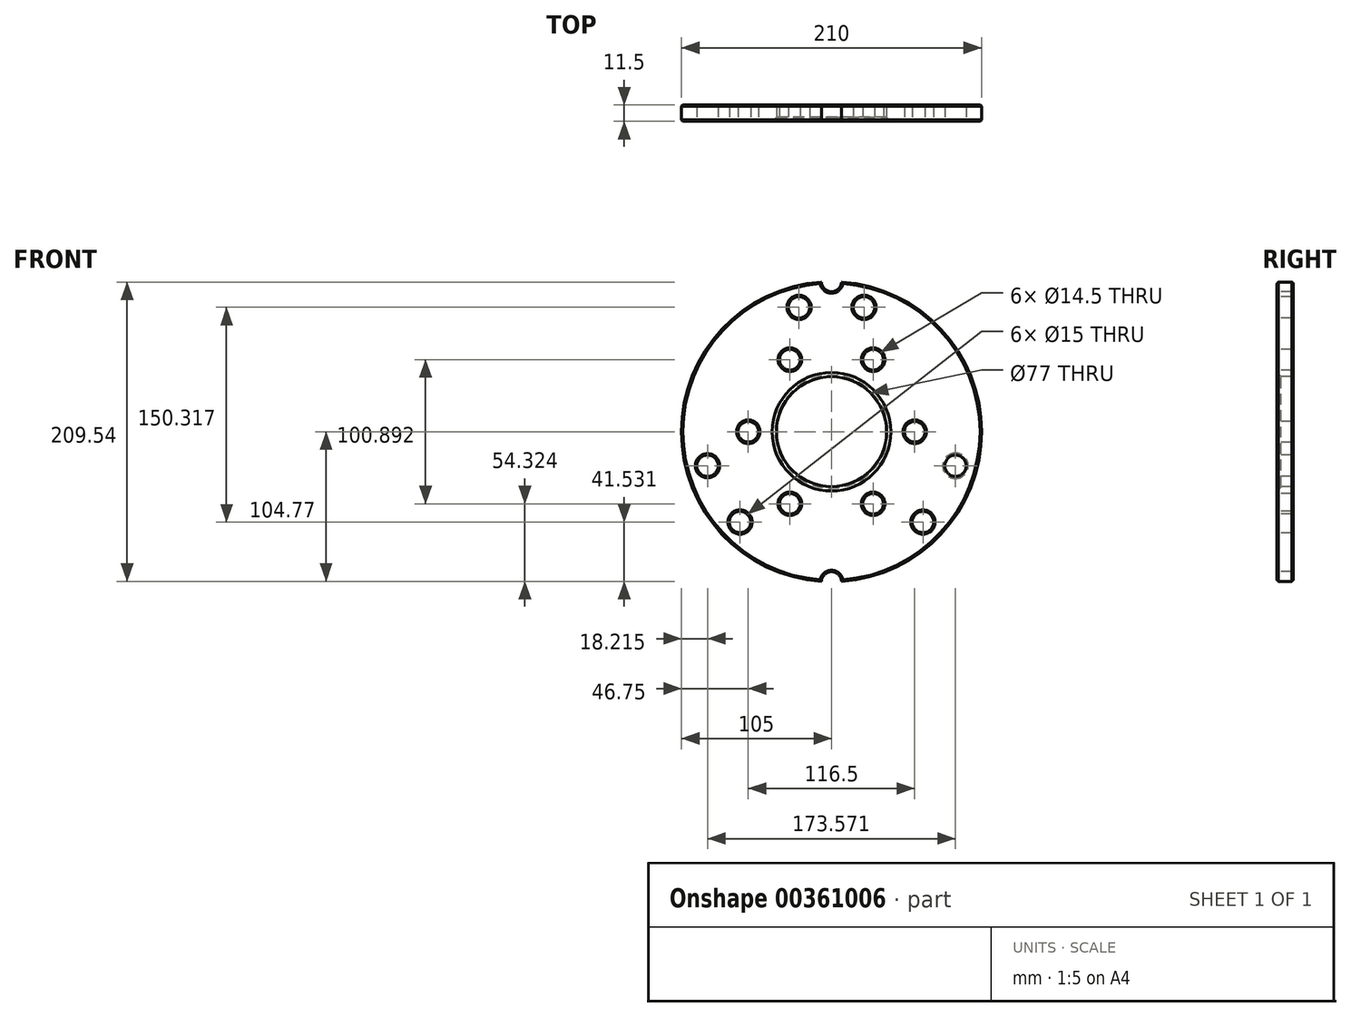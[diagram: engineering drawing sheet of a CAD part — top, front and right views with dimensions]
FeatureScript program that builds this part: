
annotation { "Feature Type Name" : "Feature", "Feature Type Description" : "" }
export const myFeature = defineFeature(function(context is Context, id is Id, definition is map)
    precondition{}
    {
        {
            var Q0;
            Q0=qCreatedBy(makeId("Front.planeOp"),FACE);
            var sketch = newSketch(context, id + "F0", { "sketchPlane" : qUnion([Q0])});
            skArc(sketch, "E0", {"start": v(-7, 104.77) * mm, "mid": v(-105, 0) * mm, "end": v(-7, -104.77) * mm});
            skCircle(sketch, "E1", {"center": v(0, 0) * mm, "radius": 38.5 * mm});
            skCircle(sketch, "E2", {"center": v(-29.12, 50.45) * mm, "radius": 7.25 * mm});
            skCircle(sketch, "E3.1.0", {"center": v(-58.25, 0) * mm, "radius": 7.25 * mm});
            skCircle(sketch, "E3.2.0", {"center": v(-29.13, -50.45) * mm, "radius": 7.25 * mm});
            skCircle(sketch, "E3.3.0", {"center": v(29.12, -50.45) * mm, "radius": 7.25 * mm});
            skCircle(sketch, "E3.4.0", {"center": v(58.25, 0) * mm, "radius": 7.25 * mm});
            skCircle(sketch, "E3.5.0", {"center": v(29.12, 50.45) * mm, "radius": 7.25 * mm});
            skArc(sketch, "E4", {"start": v(-7, 104.77) * mm, "mid": v(0, 98) * mm, "end": v(7, 104.77) * mm});
            skArc(sketch, "E5", {"start": v(7, -104.77) * mm, "mid": v(0, -98) * mm, "end": v(-7, -104.77) * mm});
            skArc(sketch, "E6.trimOffspring", {"start": v(7, -104.77) * mm, "mid": v(105, 0) * mm, "end": v(7, 104.77) * mm});
            skPoint(sketch, "E7.start.orphan", {"position": v(-105, 0) * mm});
            skCircle(sketch, "E8", {"center": v(-22.75, 87.08) * mm, "radius": 7.5 * mm});
            skCircle(sketch, "E9.1.0", {"center": v(-64.04, -63.24) * mm, "radius": 7.5 * mm});
            skCircle(sketch, "E9.2.0", {"center": v(86.79, -23.84) * mm, "radius": 7.5 * mm});
            skCircle(sketch, "E10", {"center": v(22.75, 87.08) * mm, "radius": 7.5 * mm});
            skCircle(sketch, "E11.1.0", {"center": v(-86.79, -23.84) * mm, "radius": 7.5 * mm});
            skCircle(sketch, "E11.2.0", {"center": v(64.04, -63.24) * mm, "radius": 7.5 * mm});
            skSolve(sketch);
        }
        {
            var Q0;
            Q0=makeQuery(id+"F0.imprint","IMPRINT",FACE,{"disambiguationData":[TD([[makeQuery(id+"F0.imprint","IMPRINT",EDGE,{"derivedFrom":sQuery(id+"F0.wireOp",EDGE,"E0")}),1.0]])]});
            extrude(context, id + "F1", {"entities" : qUnion([Q0]), "oppositeDirection" : true, "depth" : 11.5 * mm});
        }
        {
            var Q0;
            Q0=makeQuery(id+"F1.opExtrude","CAP_EDGE",EDGE,{"disambiguationData":[OSD([sQuery(id+"F0.wireOp",EDGE,"E1")])],"isStart":true});
            chamfer(context, id + "F2", {"entities" : qUnion([Q0]), "chamferType" : ChamferType.OFFSET_ANGLE, "width" : 3 * mm, "oppositeDirection" : false, "angle" : 45 * degree, "tangentPropagation" : true});
        }
        {
            var Q0;
            Q0=makeQuery(id+"F1.opExtrude","CAP_EDGE",EDGE,{"disambiguationData":[OSD([sQuery(id+"F0.wireOp",EDGE,"E2")])],"isStart":true});
            var Q1;
            Q1=makeQuery(id+"F1.opExtrude","CAP_EDGE",EDGE,{"disambiguationData":[OSD([sQuery(id+"F0.wireOp",EDGE,"E3.5.0")])],"isStart":true});
            var Q2;
            Q2=makeQuery(id+"F1.opExtrude","CAP_EDGE",EDGE,{"disambiguationData":[OSD([sQuery(id+"F0.wireOp",EDGE,"E9.2.0")])],"isStart":false});
            var Q3;
            Q3=makeQuery(id+"F1.opExtrude","CAP_EDGE",EDGE,{"disambiguationData":[OSD([sQuery(id+"F0.wireOp",EDGE,"E3.3.0")])],"isStart":true});
            var Q4;
            Q4=makeQuery(id+"F1.opExtrude","CAP_EDGE",EDGE,{"disambiguationData":[OSD([sQuery(id+"F0.wireOp",EDGE,"E3.2.0")])],"isStart":true});
            var Q5;
            Q5=makeQuery(id+"F1.opExtrude","CAP_EDGE",EDGE,{"disambiguationData":[OSD([sQuery(id+"F0.wireOp",EDGE,"E9.1.0")])],"isStart":true});
            var Q6;
            Q6=makeQuery(id+"F1.opExtrude","CAP_EDGE",EDGE,{"disambiguationData":[OSD([sQuery(id+"F0.wireOp",EDGE,"E5")])],"isStart":true});
            var Q7;
            Q7=makeQuery(id+"F1.opExtrude","CAP_EDGE",EDGE,{"disambiguationData":[OSD([sQuery(id+"F0.wireOp",EDGE,"E11.2.0")])],"isStart":true});
            var Q8;
            Q8=makeQuery(id+"F1.opExtrude","CAP_EDGE",EDGE,{"disambiguationData":[OSD([sQuery(id+"F0.wireOp",EDGE,"E11.1.0")])],"isStart":true});
            var Q9;
            Q9=makeQuery(id+"F1.opExtrude","CAP_EDGE",EDGE,{"disambiguationData":[OSD([sQuery(id+"F0.wireOp",EDGE,"E3.1.0")])],"isStart":true});
            var Q10;
            Q10=makeQuery(id+"F1.opExtrude","CAP_EDGE",EDGE,{"disambiguationData":[OSD([sQuery(id+"F0.wireOp",EDGE,"E3.4.0")])],"isStart":true});
            var Q11;
            Q11=makeQuery(id+"F1.opExtrude","CAP_EDGE",EDGE,{"disambiguationData":[OSD([sQuery(id+"F0.wireOp",EDGE,"E8")])],"isStart":true});
            var Q12;
            Q12=makeQuery(id+"F1.opExtrude","CAP_EDGE",EDGE,{"disambiguationData":[OSD([sQuery(id+"F0.wireOp",EDGE,"E10")])],"isStart":true});
            var Q13;
            Q13=makeQuery(id+"F1.opExtrude","CAP_EDGE",EDGE,{"disambiguationData":[OSD([sQuery(id+"F0.wireOp",EDGE,"E4")])],"isStart":true});
            var Q14;
            Q14=makeQuery(id+"F1.opExtrude","CAP_EDGE",EDGE,{"disambiguationData":[OSD([sQuery(id+"F0.wireOp",EDGE,"E6.trimOffspring")])],"isStart":true});
            var Q15;
            Q15=makeQuery(id+"F1.opExtrude","CAP_EDGE",EDGE,{"disambiguationData":[OSD([sQuery(id+"F0.wireOp",EDGE,"E0")])],"isStart":true});
            chamfer(context, id + "F3", {"entities" : qUnion([Q0, Q1, Q2, Q3, Q4, Q5, Q6, Q7, Q8, Q9, Q10, Q11, Q12, Q13, Q14, Q15]), "chamferType" : ChamferType.OFFSET_ANGLE, "width" : 1 * mm, "oppositeDirection" : false, "angle" : 45 * degree, "tangentPropagation" : true});
        }
        {
            var Q0;
            Q0=makeQuery(id+"F1.opExtrude","CAP_FACE",FACE,{"disambiguationData":[OSD([sQuery(id+"F0.wireOp",EDGE,"E0"),sQuery(id+"F0.wireOp",EDGE,"E1"),sQuery(id+"F0.wireOp",EDGE,"E2"),sQuery(id+"F0.wireOp",EDGE,"E3.1.0"),sQuery(id+"F0.wireOp",EDGE,"E3.2.0"),sQuery(id+"F0.wireOp",EDGE,"E3.3.0"),sQuery(id+"F0.wireOp",EDGE,"E3.4.0"),sQuery(id+"F0.wireOp",EDGE,"E3.5.0"),sQuery(id+"F0.wireOp",EDGE,"E4"),sQuery(id+"F0.wireOp",EDGE,"E5"),sQuery(id+"F0.wireOp",EDGE,"E6.trimOffspring"),sQuery(id+"F0.wireOp",EDGE,"E8"),sQuery(id+"F0.wireOp",EDGE,"E9.1.0"),sQuery(id+"F0.wireOp",EDGE,"E9.2.0"),sQuery(id+"F0.wireOp",EDGE,"E10"),sQuery(id+"F0.wireOp",EDGE,"E11.1.0"),sQuery(id+"F0.wireOp",EDGE,"E11.2.0")])],"isStart":false});
            chamfer(context, id + "F4", {"entities" : qUnion([Q0]), "chamferType" : ChamferType.OFFSET_ANGLE, "width" : 1 * mm, "oppositeDirection" : false, "angle" : 45 * degree, "tangentPropagation" : true});
        }
    });
